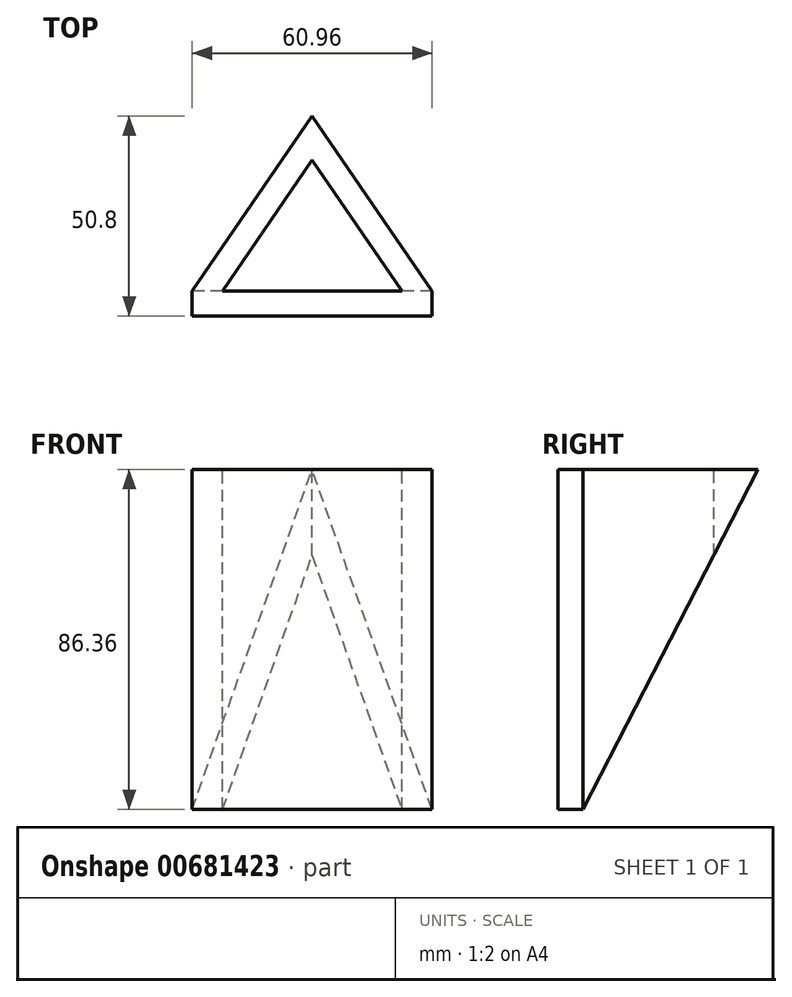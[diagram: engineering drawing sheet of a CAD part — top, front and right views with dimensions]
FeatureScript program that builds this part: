
annotation { "Feature Type Name" : "Feature", "Feature Type Description" : "" }
export const myFeature = defineFeature(function(context is Context, id is Id, definition is map)
    precondition{}
    {
        {
            var Q0;
            Q0=qCreatedBy(makeId("Front.planeOp"),FACE);
            var sketch = newSketch(context, id + "F0", { "sketchPlane" : qUnion([Q0])});
            skLineSegment(sketch, "E0.bottom", {"start": v(30.48, -43.18) * mm, "end": v(-30.48, -43.18) * mm});
            skLineSegment(sketch, "E0.top", {"start": v(30.48, 43.18) * mm, "end": v(-30.48, 43.18) * mm});
            skLineSegment(sketch, "E0.left", {"start": v(30.48, -43.18) * mm, "end": v(30.48, 43.18) * mm});
            skLineSegment(sketch, "E0.right", {"start": v(-30.48, -43.18) * mm, "end": v(-30.48, 43.18) * mm});
            skPoint(sketch, "E0.middle", {"position": v(0, 0) * mm});
            skSolve(sketch);
        }
        {
            var Q0;
            Q0 = qSketchRegion(id + "F0", true);
            extrude(context, id + "F1", {"entities" : qUnion([Q0]), "oppositeDirection" : true, "depth" : 6.35 * mm, "offsetDistance" : 25.4 * mm});
        }
        {
            var Q0;
            Q0=qCreatedBy(makeId("Front.planeOp"),FACE);
            cPlane(context, id + "F2", {"entities" : qUnion([Q0]), "cplaneType" : CPlaneType.OFFSET, "offset" : 50.8 * mm, "oppositeDirection" : true, "width" : 152.4 * mm, "height" : 152.4 * mm});
        }
        {
            var Q0;
            Q0=qCreatedBy(id+"F2.planeOp",FACE);
            var sketch = newSketch(context, id + "F3", { "sketchPlane" : qUnion([Q0])});
            skPoint(sketch, "E1.0", {"position": v(0, 43.18) * mm});
            skPoint(sketch, "E2.0", {"position": v(0, -43.18) * mm});
            skLineSegment(sketch, "E3", {"start": v(0, 43.18) * mm, "end": v(0, -43.18) * mm});
            skSolve(sketch);
        }
        {
            var Q1;
            Q1=makeQuery(id+"F1.opExtrude","CAP_FACE",FACE,{"disambiguationData":[OSD([sQuery(id+"F0.wireOp",EDGE,"E0.bottom"),sQuery(id+"F0.wireOp",EDGE,"E0.top"),sQuery(id+"F0.wireOp",EDGE,"E0.left"),sQuery(id+"F0.wireOp",EDGE,"E0.right")])],"isStart":false});
            var Q2;
            Q2=sQuery(id+"F3.wireOp",VERTEX,"E1.0");
            loft(context, id + "F4", {"operationType" : NewBodyOperationType.ADD, "sheetProfilesArray" : [{ "sheetProfileEntities" : qUnion([Q1]) }, { "sheetProfileEntities" : qUnion([Q2]) }]});
        }
        {
            var Q0;
            {var subQ0=sQuery(id+"F0.wireOp",EDGE,"E0.top");Q0=makeQuery(id+"F4.boolean.opBoolean","MERGE",FACE,{"derivedFrom":[makeQuery(id+"F1.opExtrude","SWEPT_FACE",FACE,{"disambiguationData":[OSD([subQ0])]}),makeQuery(id+"F4.opLoft","SWEPT_FACE",FACE,{"disambiguationData":[OSD([subQ0,sQuery(id+"F0.wireOp",EDGE,"E0.left"),sQuery(id+"F0.wireOp",EDGE,"E0.right")])]})]});}
            var sketch = newSketch(context, id + "F5", { "sketchPlane" : qUnion([Q0])});
            skLineSegment(sketch, "E4.0", {"start": v(-22.78, 6.35) * mm, "end": v(22.78, 6.35) * mm});
            skLineSegment(sketch, "E4.1", {"start": v(0, 39.57) * mm, "end": v(-22.78, 6.35) * mm});
            skLineSegment(sketch, "E4.2", {"start": v(22.78, 6.35) * mm, "end": v(0, 39.57) * mm});
            skSolve(sketch);
        }
        {
            var Q0;
            Q0=makeQuery(id+"F5.imprint","IMPRINT",FACE,{"disambiguationData":[TD([[makeQuery(id+"F5.imprint","IMPRINT",EDGE,{"derivedFrom":sQuery(id+"F5.wireOp",EDGE,"E4.0")}),1.0]])]});
            extrude(context, id + "F6", {"entities" : qUnion([Q0]), "operationType" : NewBodyOperationType.REMOVE, "endBound" : BoundingType.THROUGH_ALL, "oppositeDirection" : true, "depth" : 25.4 * mm, "offsetDistance" : 25.4 * mm});
        }
    });
